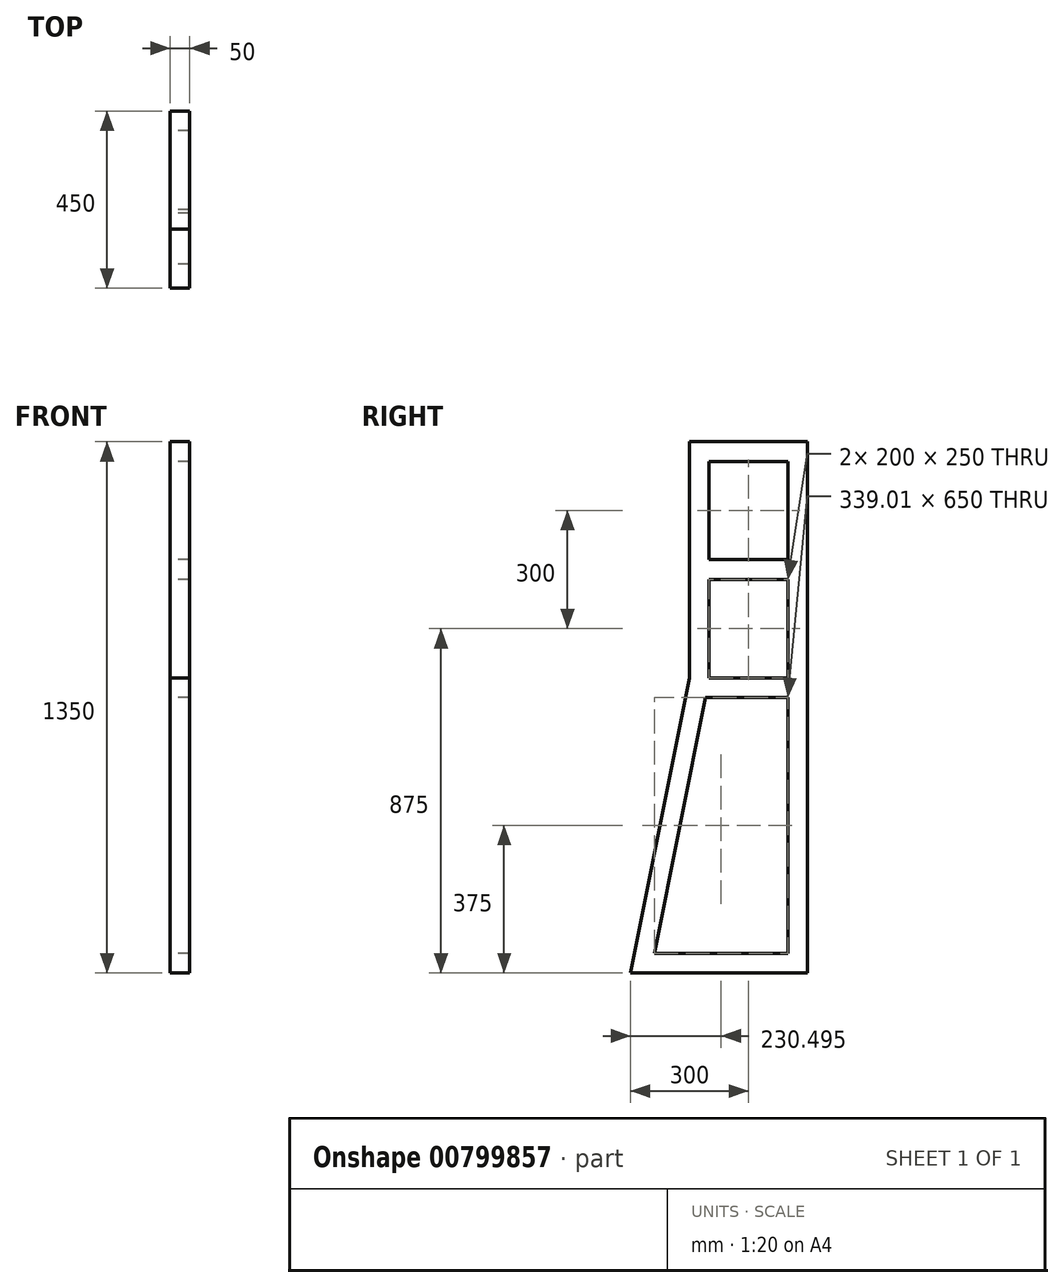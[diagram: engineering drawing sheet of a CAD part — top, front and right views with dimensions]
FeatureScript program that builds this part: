
annotation { "Feature Type Name" : "Feature", "Feature Type Description" : "" }
export const myFeature = defineFeature(function(context is Context, id is Id, definition is map)
    precondition{}
    {
        {
            var Q0;
            Q0=qCreatedBy(makeId("Right.planeOp"),FACE);
            var sketch = newSketch(context, id + "F0", { "sketchPlane" : qUnion([Q0])});
            skLineSegment(sketch, "E0", {"start": v(0, 0) * mm, "end": v(-338.45, 0) * mm});
            skLineSegment(sketch, "E1", {"start": v(0, 1000) * mm, "end": v(0, 0) * mm});
            skLineSegment(sketch, "E2.bottom", {"start": v(-389, 50) * mm, "end": v(-50, 50) * mm});
            skLineSegment(sketch, "E2.right", {"start": v(-50, 50) * mm, "end": v(-50, 700) * mm});
            skPoint(sketch, "E2.middle", {"position": v(-219.5, 375) * mm});
            skLineSegment(sketch, "E3.bottom", {"start": v(-250, 750) * mm, "end": v(-50, 750) * mm});
            skLineSegment(sketch, "E3.top", {"start": v(-250, 1000) * mm, "end": v(-50, 1000) * mm});
            skLineSegment(sketch, "E3.left", {"start": v(-250, 750) * mm, "end": v(-250, 1000) * mm});
            skLineSegment(sketch, "E3.right", {"start": v(-50, 750) * mm, "end": v(-50, 1000) * mm});
            skPoint(sketch, "E3.middle", {"position": v(-150, 875) * mm});
            skLineSegment(sketch, "E4", {"start": v(-300, 1050) * mm, "end": v(-300, 750) * mm});
            skLineSegment(sketch, "E5", {"start": v(-450, 0) * mm, "end": v(-338.45, 0) * mm});
            skLineSegment(sketch, "E6", {"start": v(-389, 50) * mm, "end": v(-259, 700) * mm});
            skLineSegment(sketch, "E7", {"start": v(-300, 750) * mm, "end": v(-450, 0) * mm});
            skLineSegment(sketch, "E8", {"start": v(-50, 700) * mm, "end": v(-259, 700) * mm});
            skLineSegment(sketch, "E9", {"start": v(0, 1000) * mm, "end": v(0, 1350) * mm});
            skLineSegment(sketch, "E10", {"start": v(0, 1350) * mm, "end": v(-300, 1350) * mm});
            skLineSegment(sketch, "E11", {"start": v(-300, 1350) * mm, "end": v(-300, 1050) * mm});
            skLineSegment(sketch, "E12.bottom", {"start": v(-250, 1050) * mm, "end": v(-50, 1050) * mm});
            skLineSegment(sketch, "E12.top", {"start": v(-250, 1300) * mm, "end": v(-50, 1300) * mm});
            skLineSegment(sketch, "E12.left", {"start": v(-250, 1050) * mm, "end": v(-250, 1300) * mm});
            skLineSegment(sketch, "E12.right", {"start": v(-50, 1050) * mm, "end": v(-50, 1300) * mm});
            skPoint(sketch, "E12.middle", {"position": v(-150, 1175) * mm});
            skPoint(sketch, "E12.middle.positionSnap0", {"position": v(0, 1175) * mm});
            skPoint(sketch, "E12.centerSnap0", {"position": v(0, 1175) * mm});
            skSolve(sketch);
        }
        {
            var Q0;
            Q0=makeQuery(id+"F0.imprint","IMPRINT",FACE,{"disambiguationData":[TD([[makeQuery(id+"F0.imprint","IMPRINT",EDGE,{"derivedFrom":sQuery(id+"F0.wireOp",EDGE,"E0")}),-1.0]])]});
            extrude(context, id + "F1", {"entities" : qUnion([Q0]), "depth" : 50 * mm, "offsetDistance" : 25 * mm});
        }
    });
